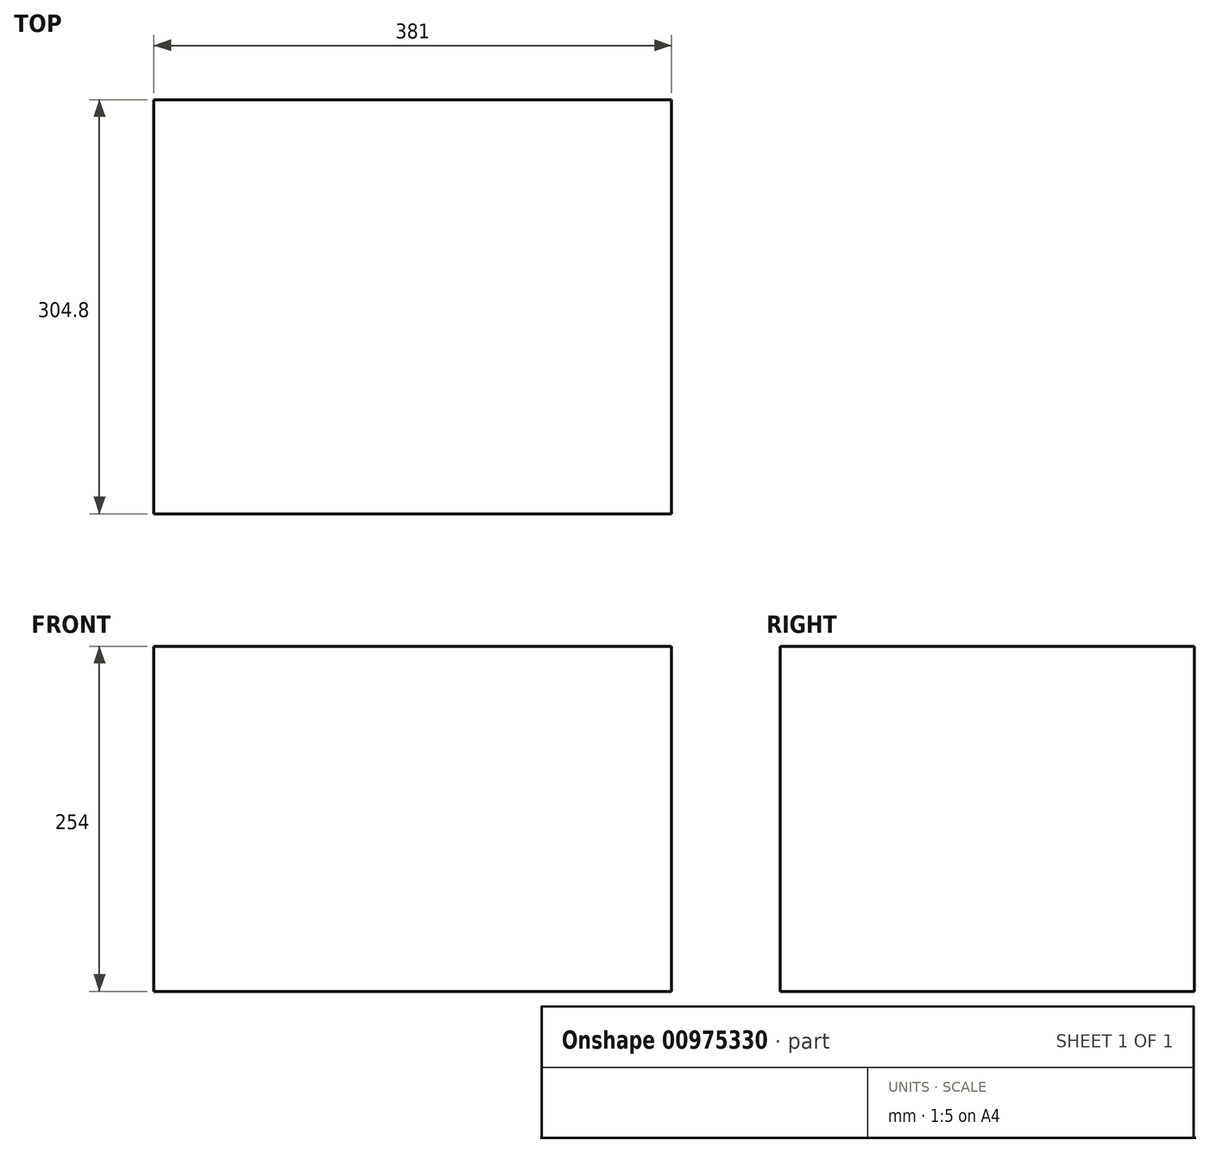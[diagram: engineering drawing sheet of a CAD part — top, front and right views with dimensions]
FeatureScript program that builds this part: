
annotation { "Feature Type Name" : "Feature", "Feature Type Description" : "" }
export const myFeature = defineFeature(function(context is Context, id is Id, definition is map)
    precondition{}
    {
        {
            var Q0;
            Q0=qCreatedBy(makeId("Top.planeOp"),FACE);
            var sketch = newSketch(context, id + "F0", { "sketchPlane" : qUnion([Q0])});
            skLineSegment(sketch, "E0.bottom", {"start": v(-303.28, 296.2) * mm, "end": v(77.72, 296.2) * mm});
            skLineSegment(sketch, "E0.top", {"start": v(-303.28, -8.6) * mm, "end": v(77.72, -8.6) * mm});
            skLineSegment(sketch, "E0.left", {"start": v(-303.28, 296.2) * mm, "end": v(-303.28, -8.6) * mm});
            skLineSegment(sketch, "E0.right", {"start": v(77.72, 296.2) * mm, "end": v(77.72, -8.6) * mm});
            skSolve(sketch);
        }
        {
            var Q0;
            Q0 = qSketchRegion(id + "F0", true);
            extrude(context, id + "F1", {"entities" : qUnion([Q0]), "depth" : 254 * mm, "offsetDistance" : 25.4 * mm});
        }
    });
